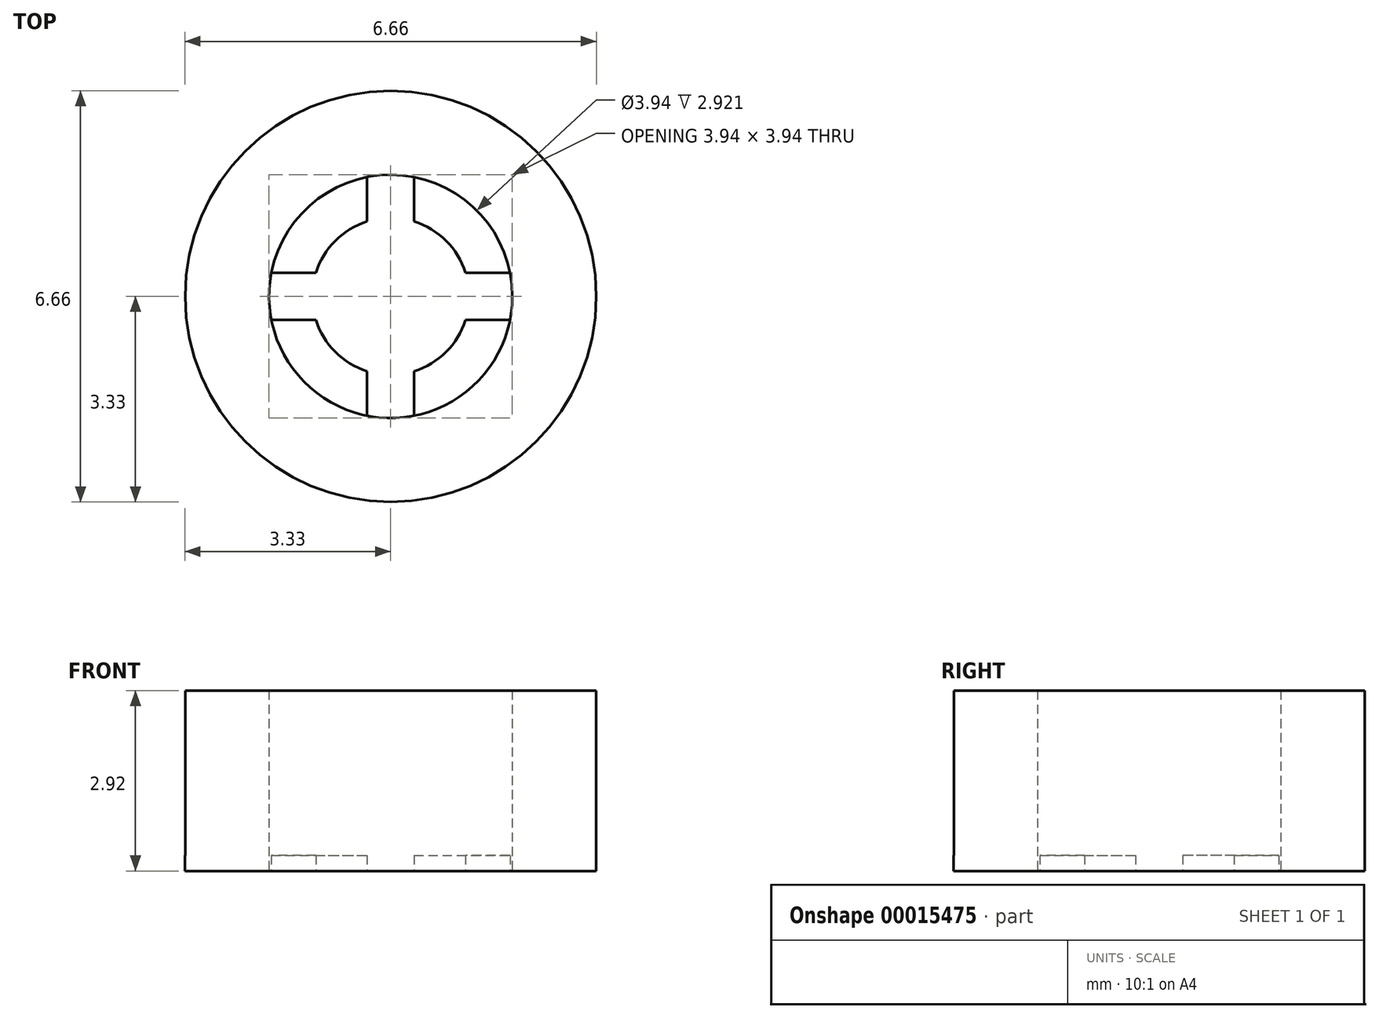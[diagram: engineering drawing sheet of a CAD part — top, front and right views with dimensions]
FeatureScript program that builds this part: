
annotation { "Feature Type Name" : "Feature", "Feature Type Description" : "" }
export const myFeature = defineFeature(function(context is Context, id is Id, definition is map)
    precondition{}
    {
        {
            var Q0;
            Q0=qCreatedBy(makeId("Top.planeOp"),FACE);
            var sketch = newSketch(context, id + "F0", { "sketchPlane" : qUnion([Q0])});
            skCircle(sketch, "E0", {"center": v(0, 0) * mm, "radius": 3.33 * mm});
            skArc(sketch, "E1", {"start": v(-1.93, 0.38) * mm, "mid": v(-1.97, 0) * mm, "end": v(-1.93, -0.38) * mm});
            skLineSegment(sketch, "E2", {"start": v(-1.97, 0) * mm, "end": v(1.97, 0) * mm, "construction": true});
            skLineSegment(sketch, "E3", {"start": v(0, 1.27) * mm, "end": v(0, -1.97) * mm, "construction": true});
            skArc(sketch, "E4", {"start": v(-0.38, 1.21) * mm, "mid": v(-0.9, 0.9) * mm, "end": v(-1.21, 0.38) * mm});
            skLineSegment(sketch, "E5", {"start": v(0.38, 1.93) * mm, "end": v(0.38, 1.21) * mm});
            skLineSegment(sketch, "E6", {"start": v(-0.38, -1.93) * mm, "end": v(-0.38, -1.21) * mm});
            skLineSegment(sketch, "E7", {"start": v(-1.93, 0.38) * mm, "end": v(-1.21, 0.38) * mm});
            skLineSegment(sketch, "E8", {"start": v(1.93, -0.38) * mm, "end": v(1.21, -0.38) * mm});
            skPoint(sketch, "E9.orphan", {"position": v(0, 1.97) * mm});
            skLineSegment(sketch, "E10.trimOffspring", {"start": v(1.21, 0.38) * mm, "end": v(1.93, 0.38) * mm});
            skLineSegment(sketch, "E11.trimOffspring", {"start": v(-0.38, 1.21) * mm, "end": v(-0.38, 1.93) * mm});
            skLineSegment(sketch, "E12.trimOffspring", {"start": v(0.38, -1.21) * mm, "end": v(0.38, -1.93) * mm});
            skArc(sketch, "E13.trimOffspring", {"start": v(1.21, 0.38) * mm, "mid": v(0.9, 0.9) * mm, "end": v(0.38, 1.21) * mm});
            skArc(sketch, "E14.trimOffspring", {"start": v(0.38, -1.21) * mm, "mid": v(0.9, -0.9) * mm, "end": v(1.21, -0.38) * mm});
            skArc(sketch, "E15.trimOffspring", {"start": v(-1.21, -0.38) * mm, "mid": v(-0.9, -0.9) * mm, "end": v(-0.38, -1.21) * mm});
            skLineSegment(sketch, "E16.trimOffspring", {"start": v(-1.21, -0.38) * mm, "end": v(-1.93, -0.38) * mm});
            skArc(sketch, "E17.trimOffspring", {"start": v(0.38, 1.93) * mm, "mid": v(0, 1.97) * mm, "end": v(-0.38, 1.93) * mm});
            skArc(sketch, "E18.trimOffspring", {"start": v(1.93, -0.38) * mm, "mid": v(1.97, 0) * mm, "end": v(1.93, 0.38) * mm});
            skArc(sketch, "E19.trimOffspring", {"start": v(-0.38, -1.93) * mm, "mid": v(0, -1.97) * mm, "end": v(0.38, -1.93) * mm});
            skSolve(sketch);
        }
        {
            var Q0;
            Q0 = qSketchRegion(id + "F0", true);
            extrude(context, id + "F1", {"entities" : qUnion([Q0]), "depth" : 0.25 * mm});
        }
        {
            var Q0;
            Q0=qCreatedBy(makeId("Top.planeOp"),FACE);
            var sketch = newSketch(context, id + "F2", { "sketchPlane" : qUnion([Q0])});
            skCircle(sketch, "E20", {"center": v(0, 0) * mm, "radius": 3.33 * mm});
            skCircle(sketch, "E21", {"center": v(0, 0) * mm, "radius": 1.97 * mm});
            skSolve(sketch);
        }
        {
            var Q0;
            Q0 = qSketchRegion(id + "F2", true);
            extrude(context, id + "F3", {"entities" : qUnion([Q0]), "operationType" : NewBodyOperationType.ADD, "depth" : 2.92 * mm});
        }
    });
